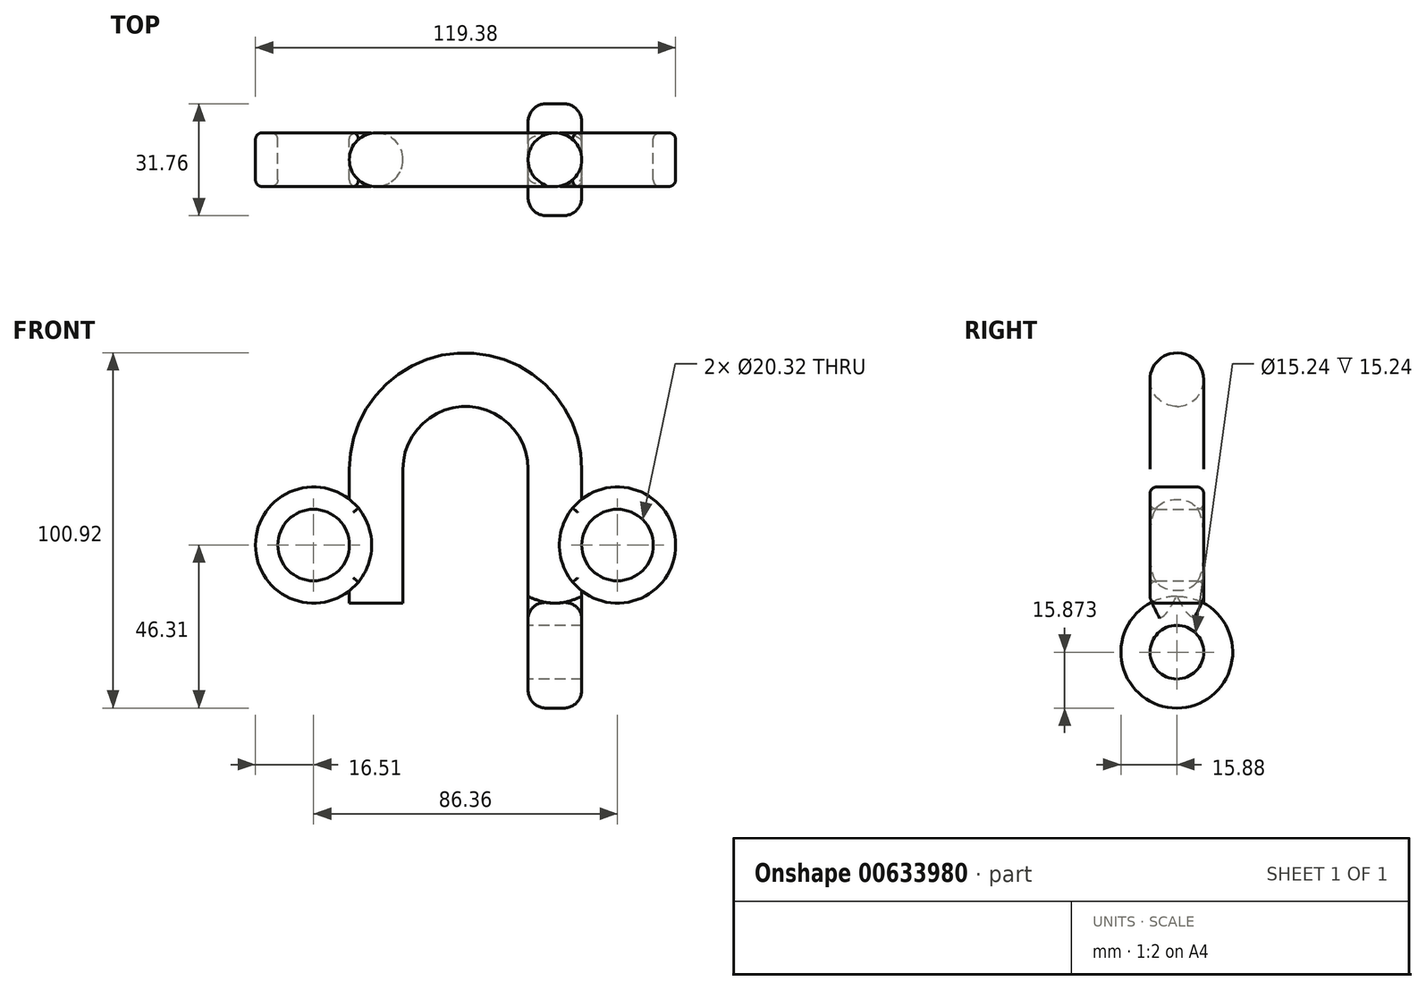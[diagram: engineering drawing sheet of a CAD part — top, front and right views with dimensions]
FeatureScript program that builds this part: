
annotation { "Feature Type Name" : "Feature", "Feature Type Description" : "" }
export const myFeature = defineFeature(function(context is Context, id is Id, definition is map)
    precondition{}
    {
        {
            var Q0;
            Q0=qCreatedBy(makeId("Front.planeOp"),FACE);
            var sketch = newSketch(context, id + "F0", { "sketchPlane" : qUnion([Q0])});
            skLineSegment(sketch, "E0", {"start": v(-25.4, 0) * mm, "end": v(-25.4, 38.1) * mm});
            skLineSegment(sketch, "E1", {"start": v(0, -23.07) * mm, "end": v(0, 59.26) * mm, "construction": true});
            skLineSegment(sketch, "E2", {"start": v(25.4, 38.1) * mm, "end": v(25.4, 0) * mm});
            skArc(sketch, "E3", {"start": v(-25.4, 38.1) * mm, "mid": v(0, 63.5) * mm, "end": v(25.4, 38.1) * mm});
            skCircle(sketch, "E4", {"center": v(43.18, 16.51) * mm, "radius": 10.16 * mm});
            skCircle(sketch, "E5", {"center": v(-43.18, 16.51) * mm, "radius": 10.16 * mm});
            skLineSegment(sketch, "E6", {"start": v(-61.56, 0) * mm, "end": v(59.1, 0) * mm, "construction": true});
            skCircle(sketch, "E7", {"center": v(-43.18, 16.51) * mm, "radius": 16.51 * mm});
            skCircle(sketch, "E8", {"center": v(43.18, 16.51) * mm, "radius": 16.51 * mm});
            skSolve(sketch);
        }
        {
            var Q0;
            Q0=qCreatedBy(makeId("Top.planeOp"),FACE);
            var sketch = newSketch(context, id + "F1", { "sketchPlane" : qUnion([Q0])});
            skCircle(sketch, "E9", {"center": v(-25.4, 0) * mm, "radius": 7.62 * mm});
            skCircle(sketch, "E10", {"center": v(25.4, 0) * mm, "radius": 7.62 * mm});
            skSolve(sketch);
        }
        {
            var Q0;
            Q0=makeQuery(id+"F1.imprint","IMPRINT",FACE,{"disambiguationData":[TD([[makeQuery(id+"F1.imprint","IMPRINT",EDGE,{"derivedFrom":sQuery(id+"F1.wireOp",EDGE,"E9")}),1.0]])]});
            var Q1;
            Q1=sQuery(id+"F0.wireOp",EDGE,"E0");
            var Q2;
            Q2=sQuery(id+"F0.wireOp",EDGE,"E3");
            var Q3;
            Q3=sQuery(id+"F0.wireOp",EDGE,"E2");
            sweep(context, id + "F2", {"profiles" : qUnion([Q0]), "path" : qUnion([Q1, Q2, Q3])});
        }
        {
            var Q0;
            Q0 = qSketchRegion(id + "F0", true);
            extrude(context, id + "F3", {"entities" : qUnion([Q0]), "operationType" : NewBodyOperationType.ADD, "endBound" : BoundingType.SYMMETRIC, "depth" : 15.24 * mm, "offsetDistance" : 25.4 * mm});
        }
        {
            var Q0;
            Q0=makeQuery(id+"F3.opExtrude","CAP_EDGE",EDGE,{"disambiguationData":[OSD([sQuery(id+"F0.wireOp",EDGE,"E5")])],"isStart":false});
            fillet(context, id + "F4", {"entities" : qUnion([Q0]), "radius" : 1.9 * mm, "tangentPropagation" : true, "allowEdgeOverflow" : false});
        }
        {
            var Q0;
            Q0=makeQuery(id+"F3.opExtrude","CAP_EDGE",EDGE,{"disambiguationData":[OSD([sQuery(id+"F0.wireOp",EDGE,"E5")])],"isStart":true});
            fillet(context, id + "F5", {"entities" : qUnion([Q0]), "radius" : 1.9 * mm, "tangentPropagation" : true, "allowEdgeOverflow" : false});
        }
        {
            var Q0;
            Q0=makeQuery(id+"F3.opExtrude","CAP_EDGE",EDGE,{"disambiguationData":[OSD([sQuery(id+"F0.wireOp",EDGE,"E7")])],"isStart":true});
            var Q1;
            Q1=makeQuery(id+"F3.opExtrude","CAP_EDGE",EDGE,{"disambiguationData":[OSD([sQuery(id+"F0.wireOp",EDGE,"E7")])],"isStart":false});
            var Q2;
            Q2=makeQuery(id+"F3.opExtrude","CAP_EDGE",EDGE,{"disambiguationData":[OSD([sQuery(id+"F0.wireOp",EDGE,"E8")])],"isStart":true});
            var Q3;
            Q3=makeQuery(id+"F3.opExtrude","CAP_EDGE",EDGE,{"disambiguationData":[OSD([sQuery(id+"F0.wireOp",EDGE,"E8")])],"isStart":false});
            var Q4;
            Q4=makeQuery(id+"F3.opExtrude","CAP_EDGE",EDGE,{"disambiguationData":[OSD([sQuery(id+"F0.wireOp",EDGE,"E4")])],"isStart":false});
            var Q5;
            Q5=makeQuery(id+"F3.opExtrude","CAP_EDGE",EDGE,{"disambiguationData":[OSD([sQuery(id+"F0.wireOp",EDGE,"E4")])],"isStart":true});
            fillet(context, id + "F6", {"entities" : qUnion([Q0, Q1, Q2, Q3, Q4, Q5]), "radius" : 1.9 * mm, "tangentPropagation" : true, "allowEdgeOverflow" : false});
        }
        {
            var Q0;
            Q0=qCreatedBy(makeId("Right.planeOp"),FACE);
            cPlane(context, id + "F7", {"entities" : qUnion([Q0]), "cplaneType" : CPlaneType.OFFSET, "offset" : 25.4 * mm, "width" : 152.4 * mm, "height" : 152.4 * mm});
        }
        {
            var Q0;
            Q0=qCreatedBy(id+"F7.planeOp",FACE);
            var sketch = newSketch(context, id + "F8", { "sketchPlane" : qUnion([Q0])});
            skLineSegment(sketch, "E11", {"start": v(-7.62, 3.47) * mm, "end": v(0, 3.47) * mm, "construction": true});
            skLineSegment(sketch, "E12", {"start": v(0, 0) * mm, "end": v(-7.62, 0) * mm});
            skCircle(sketch, "E13", {"center": v(0, -13.93) * mm, "radius": 7.62 * mm});
            skCircle(sketch, "E14", {"center": v(0, -13.93) * mm, "radius": 15.88 * mm});
            skPoint(sketch, "E15", {"position": v(-7.62, 0) * mm});
            skLineSegment(sketch, "E16", {"start": v(0, 0) * mm, "end": v(7.62, 0) * mm, "construction": true});
            skSolve(sketch);
        }
        {
            var Q0;
            Q0 = qSketchRegion(id + "F8", true);
            extrude(context, id + "F9", {"entities" : qUnion([Q0]), "operationType" : NewBodyOperationType.ADD, "endBound" : BoundingType.SYMMETRIC, "depth" : 15.24 * mm, "offsetDistance" : 25.4 * mm});
        }
        {
            var Q0;
            Q0=makeQuery(id+"F9.opExtrude","CAP_EDGE",EDGE,{"disambiguationData":[OSD([sQuery(id+"F8.wireOp",EDGE,"E14")])],"isStart":true});
            var Q1;
            Q1=makeQuery(id+"F9.opExtrude","CAP_EDGE",EDGE,{"disambiguationData":[OSD([sQuery(id+"F8.wireOp",EDGE,"E14")])],"isStart":false});
            fillet(context, id + "F10", {"entities" : qUnion([Q0, Q1]), "radius" : 5.08 * mm, "tangentPropagation" : true, "allowEdgeOverflow" : false});
        }
        {
            var Q0;
            Q0=makeQuery(id+"F2.opSweep","SWEPT_BODY",BODY,{"disambiguationData":[OSD([sQuery(id+"F0.wireOp",EDGE,"E2"),sQuery(id+"F1.wireOp",EDGE,"E9")])]});
            var Q1;
            Q1=makeQuery(id+"F2.opSweep","SWEPT_FACE",FACE,{"disambiguationData":[OSD([sQuery(id+"F0.wireOp",EDGE,"E3"),sQuery(id+"F1.wireOp",EDGE,"E9")])]});
            transform(context, id + "F11", {"entities" : qUnion([Q0]), "transformType" : TransformType.ROTATION, "transformAxis" : qUnion([Q1]), "angle" : 90 * degree, "makeCopy" : true});
        }
        {
            var Q0;
            Q0=makeQuery(id+"F11.opPattern","COPY",BODY,{"derivedFrom":makeQuery(id+"F2.opSweep","SWEPT_BODY",BODY,{"disambiguationData":[OSD([sQuery(id+"F0.wireOp",EDGE,"E2"),sQuery(id+"F1.wireOp",EDGE,"E9")])]}),"instanceName":"1"});
            deleteBodies(context, id + "F12", {"entities" : qUnion([Q0])});
        }
    });
